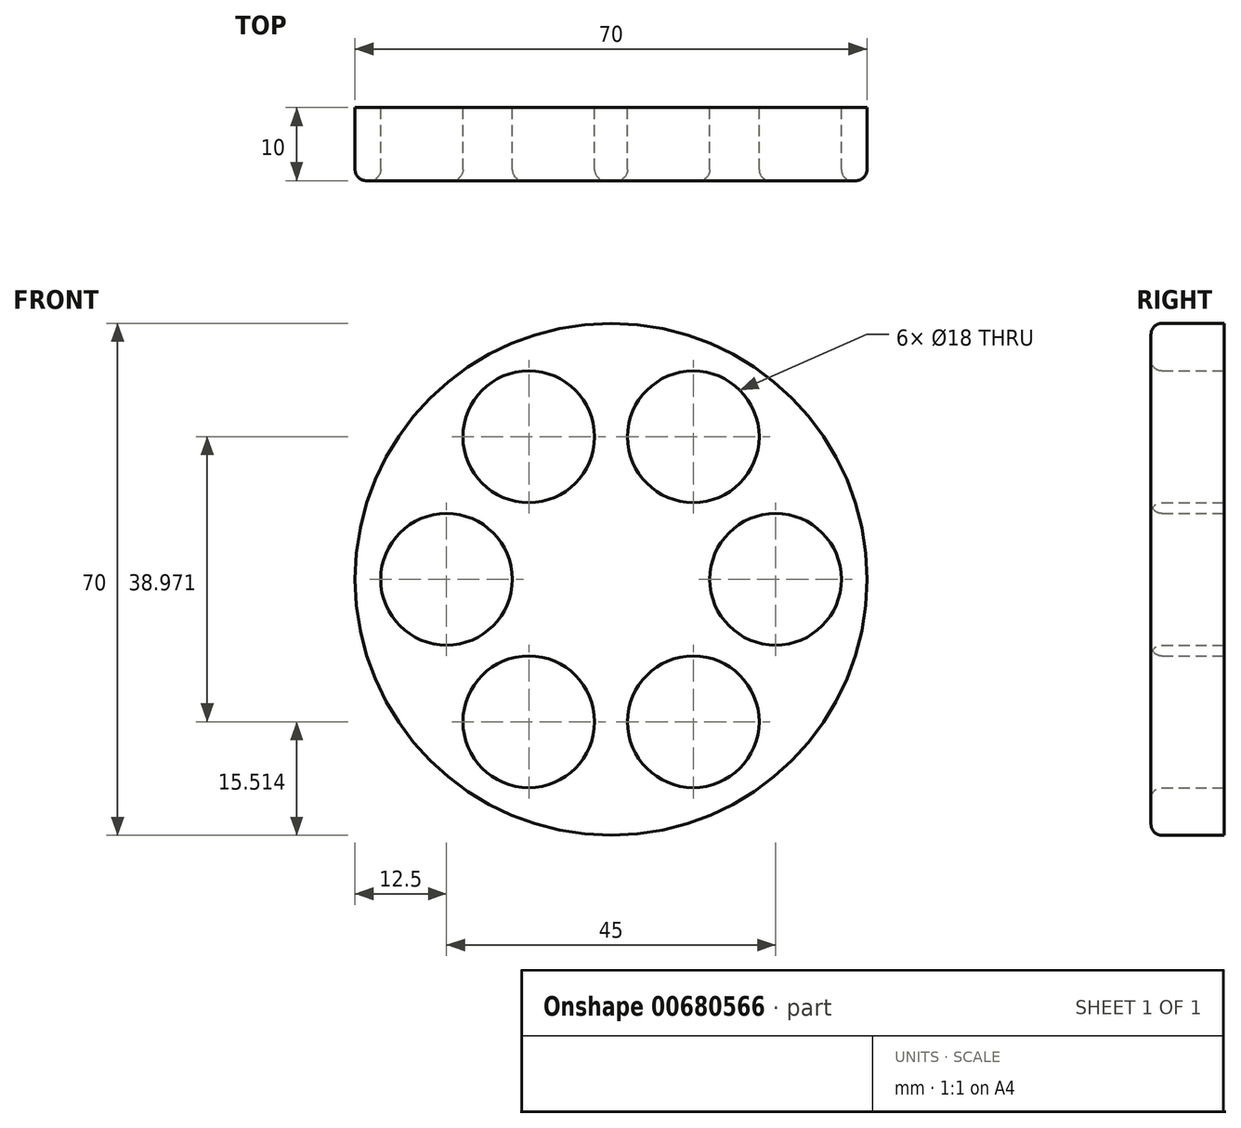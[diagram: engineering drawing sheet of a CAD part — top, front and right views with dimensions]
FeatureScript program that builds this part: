
annotation { "Feature Type Name" : "Feature", "Feature Type Description" : "" }
export const myFeature = defineFeature(function(context is Context, id is Id, definition is map)
    precondition{}
    {
        {
            var Q0;
            Q0=qCreatedBy(makeId("Front.planeOp"),FACE);
            var sketch = newSketch(context, id + "F0", { "sketchPlane" : qUnion([Q0])});
            skCircle(sketch, "E0", {"center": v(0, 0) * mm, "radius": 35 * mm});
            skCircle(sketch, "E1", {"center": v(-22.5, 0) * mm, "radius": 9 * mm});
            skCircle(sketch, "E2.1.0", {"center": v(-11.25, -19.49) * mm, "radius": 9 * mm});
            skCircle(sketch, "E2.2.0", {"center": v(11.25, -19.49) * mm, "radius": 9 * mm});
            skCircle(sketch, "E2.3.0", {"center": v(22.5, 0) * mm, "radius": 9 * mm});
            skCircle(sketch, "E2.4.0", {"center": v(11.25, 19.49) * mm, "radius": 9 * mm});
            skCircle(sketch, "E2.5.0", {"center": v(-11.25, 19.49) * mm, "radius": 9 * mm});
            skSolve(sketch);
        }
        {
            var Q0;
            Q0 = qSketchRegion(id + "F0", true);
            extrude(context, id + "F1", {"entities" : qUnion([Q0]), "depth" : 10 * mm, "offsetDistance" : 25 * mm});
        }
        {
            var Q0;
            Q0=makeQuery(id+"F1.opExtrude","CAP_EDGE",EDGE,{"disambiguationData":[OSD([sQuery(id+"F0.wireOp",EDGE,"E0")])],"isStart":false});
            var Q1;
            Q1=makeQuery(id+"F1.opExtrude","CAP_EDGE",EDGE,{"disambiguationData":[OSD([sQuery(id+"F0.wireOp",EDGE,"E2.5.0")])],"isStart":false});
            var Q2;
            Q2=makeQuery(id+"F1.opExtrude","CAP_EDGE",EDGE,{"disambiguationData":[OSD([sQuery(id+"F0.wireOp",EDGE,"E1")])],"isStart":false});
            var Q3;
            Q3=makeQuery(id+"F1.opExtrude","CAP_EDGE",EDGE,{"disambiguationData":[OSD([sQuery(id+"F0.wireOp",EDGE,"E2.4.0")])],"isStart":false});
            var Q4;
            Q4=makeQuery(id+"F1.opExtrude","CAP_EDGE",EDGE,{"disambiguationData":[OSD([sQuery(id+"F0.wireOp",EDGE,"E2.3.0")])],"isStart":false});
            var Q5;
            Q5=makeQuery(id+"F1.opExtrude","CAP_EDGE",EDGE,{"disambiguationData":[OSD([sQuery(id+"F0.wireOp",EDGE,"E2.2.0")])],"isStart":false});
            var Q6;
            Q6=makeQuery(id+"F1.opExtrude","CAP_EDGE",EDGE,{"disambiguationData":[OSD([sQuery(id+"F0.wireOp",EDGE,"E2.1.0")])],"isStart":false});
            fillet(context, id + "F2", {"entities" : qUnion([Q0, Q1, Q2, Q3, Q4, Q5, Q6]), "radius" : 1.5 * mm, "tangentPropagation" : true, "allowEdgeOverflow" : false});
        }
    });
